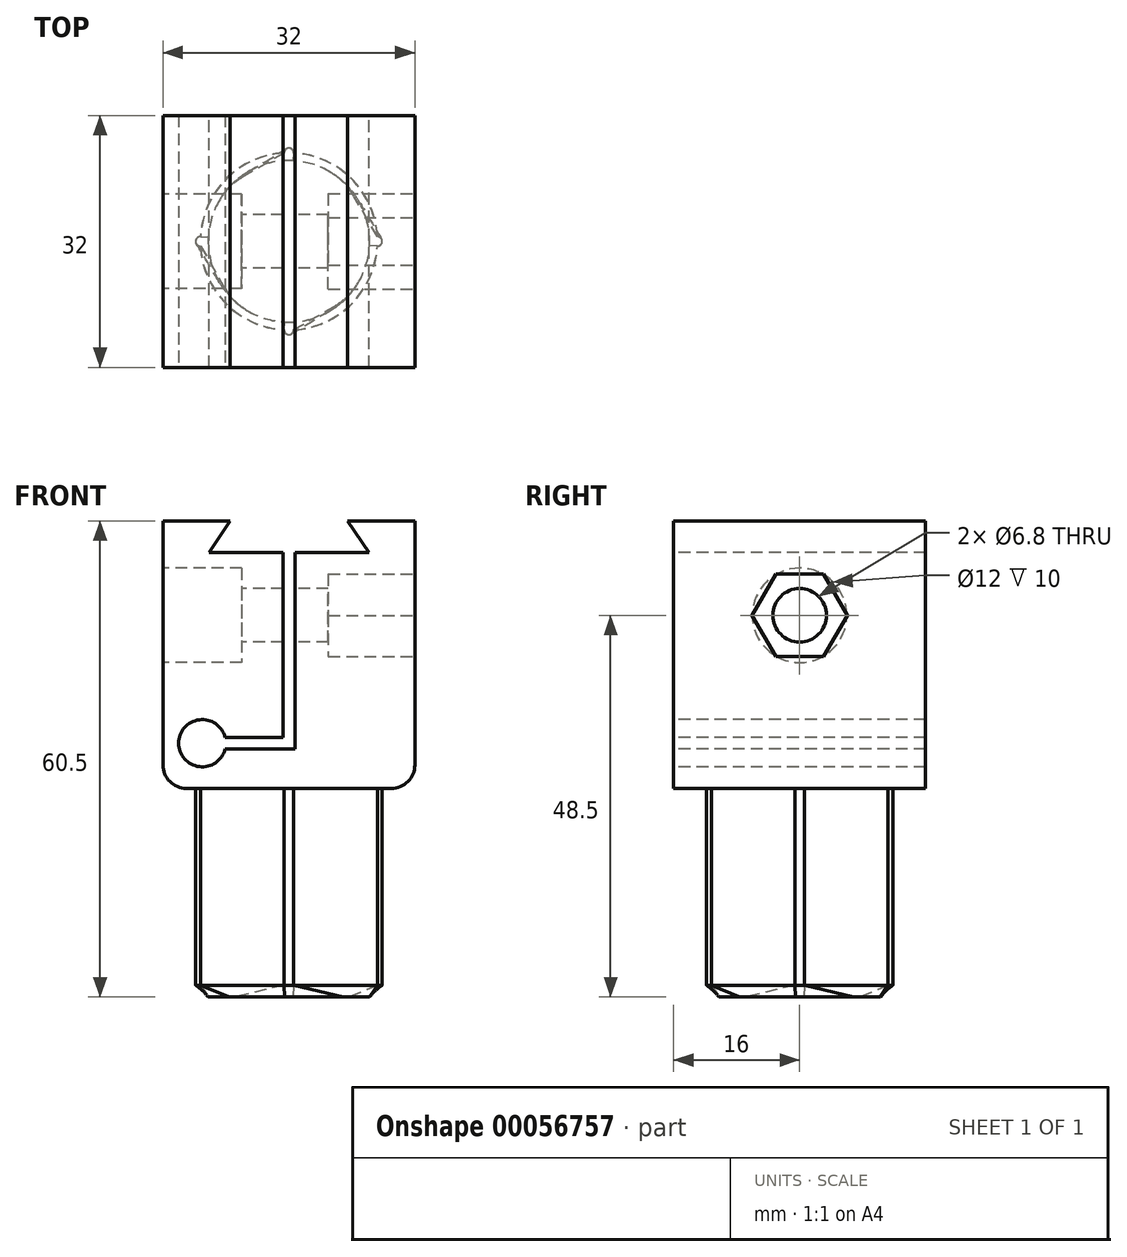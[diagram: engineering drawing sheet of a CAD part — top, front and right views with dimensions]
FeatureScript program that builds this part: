
annotation { "Feature Type Name" : "Feature", "Feature Type Description" : "" }
export const myFeature = defineFeature(function(context is Context, id is Id, definition is map)
    precondition{}
    {
        {
            var Q0;
            Q0=qCreatedBy(makeId("Front.planeOp"),FACE);
            var sketch = newSketch(context, id + "F0", { "sketchPlane" : qUnion([Q0])});
            skLineSegment(sketch, "E0", {"start": v(-16, -17) * mm, "end": v(-16, 17) * mm});
            skLineSegment(sketch, "E1", {"start": v(-16, 17) * mm, "end": v(-7.45, 17) * mm});
            skLineSegment(sketch, "E2", {"start": v(-7.45, 17) * mm, "end": v(-10.15, 13) * mm});
            skLineSegment(sketch, "E3", {"start": v(-10.15, 13) * mm, "end": v(10.15, 13) * mm});
            skLineSegment(sketch, "E4", {"start": v(10.15, 13) * mm, "end": v(7.45, 17) * mm});
            skLineSegment(sketch, "E5", {"start": v(7.45, 17) * mm, "end": v(16, 17) * mm});
            skLineSegment(sketch, "E6", {"start": v(16, 17) * mm, "end": v(16, -17) * mm});
            skLineSegment(sketch, "E7", {"start": v(16, -17) * mm, "end": v(-16, -17) * mm});
            skSolve(sketch);
        }
        {
            var Q0;
            Q0 = qSketchRegion(id + "F0", true);
            extrude(context, id + "F1", {"entities" : qUnion([Q0]), "depth" : 32 * mm});
        }
        {
            var Q0;
            Q0=makeQuery(id+"F1.opExtrude","SWEPT_FACE",FACE,{"disambiguationData":[OSD([sQuery(id+"F0.wireOp",EDGE,"E0")])]});
            var sketch = newSketch(context, id + "F2", { "sketchPlane" : qUnion([Q0])});
            skCircle(sketch, "E8", {"center": v(16, 5) * mm, "radius": 6 * mm});
            skLineSegment(sketch, "E9", {"start": v(16, 17) * mm, "end": v(16, -17) * mm, "construction": true});
            skSolve(sketch);
        }
        {
            var Q0;
            Q0 = qSketchRegion(id + "F2", true);
            extrude(context, id + "F3", {"entities" : qUnion([Q0]), "operationType" : NewBodyOperationType.REMOVE, "oppositeDirection" : true, "depth" : 10 * mm});
        }
        {
            var Q0;
            Q0=makeQuery(id+"F3.boolean.opBoolean","COPY",FACE,{"derivedFrom":makeQuery(id+"F3.opExtrude","CAP_FACE",FACE,{"disambiguationData":[OSD([sQuery(id+"F2.wireOp",EDGE,"E8")])],"isStart":false})});
            var sketch = newSketch(context, id + "F4", { "sketchPlane" : qUnion([Q0])});
            skCircle(sketch, "E10", {"center": v(16, 5) * mm, "radius": 3.4 * mm});
            skSolve(sketch);
        }
        {
            var Q0;
            Q0 = qSketchRegion(id + "F4", true);
            extrude(context, id + "F5", {"entities" : qUnion([Q0]), "operationType" : NewBodyOperationType.REMOVE, "endBound" : BoundingType.THROUGH_ALL, "oppositeDirection" : true, "depth" : 25 * mm});
        }
        {
            var Q0;
            Q0=makeQuery(id+"F1.opExtrude","CAP_FACE",FACE,{"disambiguationData":[OSD([sQuery(id+"F0.wireOp",EDGE,"E0"),sQuery(id+"F0.wireOp",EDGE,"E1"),sQuery(id+"F0.wireOp",EDGE,"E2"),sQuery(id+"F0.wireOp",EDGE,"E3"),sQuery(id+"F0.wireOp",EDGE,"E4"),sQuery(id+"F0.wireOp",EDGE,"E5"),sQuery(id+"F0.wireOp",EDGE,"E6"),sQuery(id+"F0.wireOp",EDGE,"E7")])],"isStart":false});
            var sketch = newSketch(context, id + "F6", { "sketchPlane" : qUnion([Q0])});
            skLineSegment(sketch, "E11", {"start": v(-0.75, 13) * mm, "end": v(-0.75, -10.5) * mm});
            skLineSegment(sketch, "E12", {"start": v(-0.75, -10.5) * mm, "end": v(-8.1, -10.5) * mm});
            skLineSegment(sketch, "E13", {"start": v(-8.1, -12) * mm, "end": v(0.75, -12) * mm});
            skLineSegment(sketch, "E14", {"start": v(0.75, -12) * mm, "end": v(0.75, 13) * mm});
            skLineSegment(sketch, "E15", {"start": v(0.75, 13) * mm, "end": v(-0.75, 13) * mm});
            skArc(sketch, "E16", {"start": v(-8.1, -10.5) * mm, "mid": v(-14, -11.25) * mm, "end": v(-8.1, -12) * mm});
            skLineSegment(sketch, "E17", {"start": v(-11, -11.25) * mm, "end": v(11.58, -11.25) * mm, "construction": true});
            skSolve(sketch);
        }
        {
            var Q0;
            Q0 = qSketchRegion(id + "F6", true);
            extrude(context, id + "F7", {"entities" : qUnion([Q0]), "operationType" : NewBodyOperationType.REMOVE, "endBound" : BoundingType.THROUGH_ALL, "oppositeDirection" : true, "depth" : 25 * mm});
        }
        {
            var Q0;
            Q0=makeQuery(id+"F1.opExtrude","SWEPT_FACE",FACE,{"disambiguationData":[OSD([sQuery(id+"F0.wireOp",EDGE,"E6")])]});
            var sketch = newSketch(context, id + "F8", { "sketchPlane" : qUnion([Q0])});
            skCircle(sketch, "E18.cCircle", {"center": v(-16, 5) * mm, "radius": 5.25 * mm, "construction": true});
            skLineSegment(sketch, "E18.0", {"start": v(-9.94, 5) * mm, "end": v(-12.97, -0.25) * mm});
            skLineSegment(sketch, "E18.1", {"start": v(-12.97, -0.25) * mm, "end": v(-19.03, -0.25) * mm});
            skLineSegment(sketch, "E18.2", {"start": v(-19.03, -0.25) * mm, "end": v(-22.06, 5) * mm});
            skLineSegment(sketch, "E18.3", {"start": v(-22.06, 5) * mm, "end": v(-19.03, 10.25) * mm});
            skLineSegment(sketch, "E18.4", {"start": v(-19.03, 10.25) * mm, "end": v(-12.97, 10.25) * mm});
            skLineSegment(sketch, "E18.5", {"start": v(-12.97, 10.25) * mm, "end": v(-9.94, 5) * mm});
            skPoint(sketch, "E18.0.midPoint", {"position": v(-11.45, 2.37) * mm});
            skSolve(sketch);
        }
        {
            var Q0;
            Q0 = qSketchRegion(id + "F8", true);
            extrude(context, id + "F9", {"entities" : qUnion([Q0]), "operationType" : NewBodyOperationType.REMOVE, "oppositeDirection" : true, "depth" : 11 * mm});
        }
        {
            var Q0;
            Q0=makeQuery(id+"F1.opExtrude","SWEPT_FACE",FACE,{"disambiguationData":[OSD([sQuery(id+"F0.wireOp",EDGE,"E7")])]});
            var sketch = newSketch(context, id + "F10", { "sketchPlane" : qUnion([Q0])});
            skArc(sketch, "E19", {"start": v(11.23, 16.6) * mm, "mid": v(7.95, 23.95) * mm, "end": v(0.6, 27.23) * mm});
            skLineSegment(sketch, "E20", {"start": v(-16, 16) * mm, "end": v(16, 16) * mm, "construction": true});
            skArc(sketch, "E21", {"start": v(0.6, 27.23) * mm, "mid": v(0, 27.85) * mm, "end": v(-0.6, 27.23) * mm});
            skArc(sketch, "E22", {"start": v(11.23, 15.4) * mm, "mid": v(11.85, 16) * mm, "end": v(11.23, 16.6) * mm});
            skArc(sketch, "E23", {"start": v(-11.23, 16.6) * mm, "mid": v(-11.85, 16) * mm, "end": v(-11.23, 15.4) * mm});
            skArc(sketch, "E24", {"start": v(-0.6, 4.77) * mm, "mid": v(0, 4.15) * mm, "end": v(0.6, 4.77) * mm});
            skArc(sketch, "E25.trimOffspring", {"start": v(-11.23, 15.4) * mm, "mid": v(-7.95, 8.05) * mm, "end": v(-0.6, 4.77) * mm});
            skArc(sketch, "E26.trimOffspring", {"start": v(0.6, 4.77) * mm, "mid": v(7.95, 8.05) * mm, "end": v(11.23, 15.4) * mm});
            skArc(sketch, "E27.trimOffspring", {"start": v(-0.6, 27.23) * mm, "mid": v(-7.95, 23.95) * mm, "end": v(-11.23, 16.6) * mm});
            skSolve(sketch);
        }
        {
            var Q0;
            Q0 = qSketchRegion(id + "F10", true);
            extrude(context, id + "F11", {"entities" : qUnion([Q0]), "operationType" : NewBodyOperationType.ADD, "depth" : 25 * mm});
        }
        {
            var Q0;
            Q0=makeQuery(id+"F1.opExtrude","SWEPT_EDGE",EDGE,{"disambiguationData":[OSD([sQuery(id+"F0.wireOp",EDGE,"E0"),sQuery(id+"F0.wireOp",EDGE,"E7")])]});
            fillet(context, id + "F12", {"entities" : qUnion([Q0]), "radius" : 3 * mm, "tangentPropagation" : true, "allowEdgeOverflow" : false});
        }
        {
            var Q0;
            Q0=makeQuery(id+"F1.opExtrude","SWEPT_EDGE",EDGE,{"disambiguationData":[OSD([sQuery(id+"F0.wireOp",EDGE,"E6"),sQuery(id+"F0.wireOp",EDGE,"E7")])]});
            fillet(context, id + "F13", {"entities" : qUnion([Q0]), "radius" : 3 * mm, "tangentPropagation" : true, "allowEdgeOverflow" : false});
        }
        {
            var Q0;
            Q0=makeQuery(id+"F11.opExtrude","CAP_FACE",FACE,{"disambiguationData":[OSD([sQuery(id+"F10.wireOp",EDGE,"E19"),sQuery(id+"F10.wireOp",EDGE,"E21"),sQuery(id+"F10.wireOp",EDGE,"E22"),sQuery(id+"F10.wireOp",EDGE,"E23"),sQuery(id+"F10.wireOp",EDGE,"E24"),sQuery(id+"F10.wireOp",EDGE,"E25.trimOffspring"),sQuery(id+"F10.wireOp",EDGE,"E26.trimOffspring"),sQuery(id+"F10.wireOp",EDGE,"E27.trimOffspring")])],"isStart":false});
            cPlane(context, id + "F14", {"entities" : qUnion([Q0]), "cplaneType" : CPlaneType.OFFSET, "offset" : 1.5 * mm, "width" : 150 * mm, "height" : 150 * mm});
        }
        {
            var Q0;
            Q0=qCreatedBy(id+"F14.planeOp",FACE);
            var sketch = newSketch(context, id + "F15", { "sketchPlane" : qUnion([Q0])});
            skCircle(sketch, "E28", {"center": v(0, 16) * mm, "radius": 10.25 * mm});
            skSolve(sketch);
        }
        {
            var Q1;
            Q1=makeQuery(id+"F11.opExtrude","CAP_FACE",FACE,{"disambiguationData":[OSD([sQuery(id+"F10.wireOp",EDGE,"E19"),sQuery(id+"F10.wireOp",EDGE,"E21"),sQuery(id+"F10.wireOp",EDGE,"E22"),sQuery(id+"F10.wireOp",EDGE,"E23"),sQuery(id+"F10.wireOp",EDGE,"E24"),sQuery(id+"F10.wireOp",EDGE,"E25.trimOffspring"),sQuery(id+"F10.wireOp",EDGE,"E26.trimOffspring"),sQuery(id+"F10.wireOp",EDGE,"E27.trimOffspring")])],"isStart":false});
            var Q2;
            Q2=makeQuery(id+"F15.imprint","IMPRINT",FACE,{"disambiguationData":[TD([[makeQuery(id+"F15.imprint","IMPRINT",EDGE,{"derivedFrom":sQuery(id+"F15.wireOp",EDGE,"E28")}),1.0]])]});
            loft(context, id + "F16", {"operationType" : NewBodyOperationType.ADD, "sheetProfilesArray" : [{ "sheetProfileEntities" : qUnion([Q1]) }, { "sheetProfileEntities" : qUnion([Q2]) }]});
        }
    });
